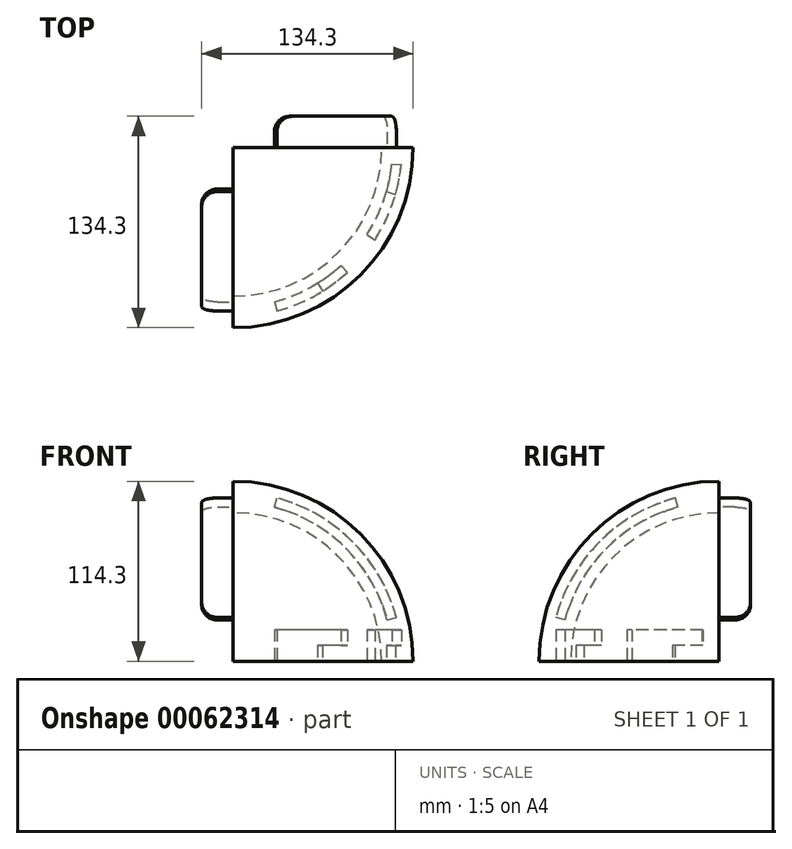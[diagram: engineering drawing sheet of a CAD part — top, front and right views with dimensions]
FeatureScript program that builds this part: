
annotation { "Feature Type Name" : "Feature", "Feature Type Description" : "" }
export const myFeature = defineFeature(function(context is Context, id is Id, definition is map)
    precondition{}
    {
        {
            var Q0;
            Q0=qCreatedBy(makeId("Right.planeOp"),FACE);
            var sketch = newSketch(context, id + "F0", { "sketchPlane" : qUnion([Q0])});
            skArc(sketch, "E0", {"start": v(0, 114.3) * mm, "mid": v(-80.82, 80.82) * mm, "end": v(-114.3, 0) * mm});
            skArc(sketch, "E1", {"start": v(0, 94.3) * mm, "mid": v(-66.68, 66.68) * mm, "end": v(-94.3, 0) * mm});
            skLineSegment(sketch, "E2", {"start": v(0, 94.3) * mm, "end": v(0, 114.3) * mm});
            skLineSegment(sketch, "E3", {"start": v(-94.3, 0) * mm, "end": v(-114.3, 0) * mm});
            skSolve(sketch);
        }
        {
            var Q0;
            Q0=makeQuery(id+"F0.imprint","IMPRINT",FACE,{"disambiguationData":[TD([[makeQuery(id+"F0.imprint","IMPRINT",EDGE,{"derivedFrom":sQuery(id+"F0.wireOp",EDGE,"E0")}),1.0]])]});
            var Q1;
            Q1=sQuery(id+"F0.wireOp",EDGE,"E2");
            revolve(context, id + "F1", {"entities" : qUnion([Q0]), "axis" : qUnion([Q1]), "revolveType" : RevolveType.ONE_DIRECTION, "angle" : 90 * degree});
        }
        {
            var Q0;
            Q0=makeQuery(id+"F1.opRevolve","CAP_FACE",FACE,{"disambiguationData":[OSD([sQuery(id+"F0.wireOp",EDGE,"E0"),sQuery(id+"F0.wireOp",EDGE,"E1"),sQuery(id+"F0.wireOp",EDGE,"E2"),sQuery(id+"F0.wireOp",EDGE,"E3")])],"isStart":false});
            var sketch = newSketch(context, id + "F2", { "sketchPlane" : qUnion([Q0])});
            skArc(sketch, "E4", {"start": v(-27.77, 103.64) * mm, "mid": v(-75.87, 75.87) * mm, "end": v(-103.64, 27.77) * mm});
            skArc(sketch, "E5", {"start": v(-26.22, 97.85) * mm, "mid": v(-71.63, 71.63) * mm, "end": v(-97.85, 26.22) * mm});
            skLineSegment(sketch, "E6", {"start": v(0, 0) * mm, "end": v(-27.77, 103.64) * mm});
            skLineSegment(sketch, "E7", {"start": v(-97.85, 26.22) * mm, "end": v(-103.64, 27.77) * mm});
            skSolve(sketch);
        }
        {
            var Q0;
            Q0=makeQuery(id+"F2.imprint","IMPRINT",FACE,{"disambiguationData":[TD([[makeQuery(id+"F2.imprint","IMPRINT",EDGE,{"derivedFrom":sQuery(id+"F2.wireOp",EDGE,"E4")}),1.0]])]});
            extrude(context, id + "F3", {"entities" : qUnion([Q0]), "operationType" : NewBodyOperationType.ADD, "depth" : 20 * mm});
        }
        {
            var Q0;
            Q0=makeQuery(id+"F0.imprint","IMPRINT",FACE,{"disambiguationData":[TD([[makeQuery(id+"F0.imprint","IMPRINT",EDGE,{"derivedFrom":sQuery(id+"F0.wireOp",EDGE,"E0")}),1.0]])]});
            var sketch = newSketch(context, id + "F4", { "sketchPlane" : qUnion([Q0])});
            skArc(sketch, "E8.0", {"start": v(-26.22, 97.85) * mm, "mid": v(-71.63, 71.63) * mm, "end": v(-97.85, 26.22) * mm});
            skArc(sketch, "E9.0", {"start": v(-27.77, 103.64) * mm, "mid": v(-75.87, 75.87) * mm, "end": v(-103.64, 27.77) * mm});
            skLineSegment(sketch, "E10", {"start": v(-26.22, 97.85) * mm, "end": v(-27.77, 103.64) * mm});
            skLineSegment(sketch, "E11", {"start": v(-97.85, 26.22) * mm, "end": v(-103.64, 27.77) * mm});
            skSolve(sketch);
        }
        {
            var Q0;
            Q0=makeQuery(id+"F4.imprint","IMPRINT",FACE,{"disambiguationData":[TD([[makeQuery(id+"F4.imprint","IMPRINT",EDGE,{"derivedFrom":sQuery(id+"F4.wireOp",EDGE,"E8.0")}),-1.0]])]});
            extrude(context, id + "F5", {"entities" : qUnion([Q0]), "operationType" : NewBodyOperationType.ADD, "oppositeDirection" : true, "depth" : 20 * mm});
        }
        {
            var Q0;
            Q0=makeQuery(id+"F5.boolean.opBoolean","MERGE",FACE,{"derivedFrom":[makeQuery(id+"F3.boolean.opBoolean","MERGE",FACE,{"derivedFrom":[makeQuery(id+"F1.opRevolve","SWEPT_FACE",FACE,{"disambiguationData":[OSD([sQuery(id+"F0.wireOp",EDGE,"E3")])]}),makeQuery(id+"F3.opExtrude","SWEPT_FACE",FACE,{"disambiguationData":[OSD([sQuery(id+"F2.wireOp",EDGE,"tj54Cu89-9J1S-AJKw-QeEM-ljXHSpR1f2pj")])]})]}),makeQuery(id+"F5.opExtrude","SWEPT_FACE",FACE,{"disambiguationData":[OSD([sQuery(id+"F4.wireOp",EDGE,"EMUQLBOC-9Rso-lLbz-JRUg-i4oPmn0DbPj1")])]})]});
            var sketch = newSketch(context, id + "F6", { "sketchPlane" : qUnion([Q0])});
            skArc(sketch, "E12", {"start": v(97.38, 27.92) * mm, "mid": v(92.18, 42) * mm, "end": v(84.96, 55.17) * mm});
            skArc(sketch, "E13", {"start": v(103.14, 29.58) * mm, "mid": v(97.64, 44.5) * mm, "end": v(89.99, 58.44) * mm});
            skLineSegment(sketch, "E14", {"start": v(26.22, 97.85) * mm, "end": v(27.77, 103.64) * mm});
            skLineSegment(sketch, "E15", {"start": v(53.68, 85.9) * mm, "end": v(56.86, 91) * mm});
            skLineSegment(sketch, "E16", {"start": v(84.96, 55.17) * mm, "end": v(89.99, 58.44) * mm});
            skLineSegment(sketch, "E17", {"start": v(97.38, 27.92) * mm, "end": v(103.14, 29.58) * mm});
            skArc(sketch, "E18.trimOffspring", {"start": v(53.68, 85.9) * mm, "mid": v(40.4, 92.9) * mm, "end": v(26.22, 97.85) * mm});
            skArc(sketch, "E19.trimOffspring", {"start": v(56.86, 91) * mm, "mid": v(42.79, 98.4) * mm, "end": v(27.77, 103.64) * mm});
            skSolve(sketch);
        }
        {
            var Q0;
            Q0=makeQuery(id+"F6.imprint","IMPRINT",FACE,{"disambiguationData":[TD([[makeQuery(id+"F6.imprint","IMPRINT",EDGE,{"derivedFrom":sQuery(id+"F6.wireOp",EDGE,"E14")}),-1.0]])]});
            var Q1;
            Q1=makeQuery(id+"F6.imprint","IMPRINT",FACE,{"disambiguationData":[TD([[makeQuery(id+"F6.imprint","IMPRINT",EDGE,{"derivedFrom":sQuery(id+"F6.wireOp",EDGE,"E12")}),-1.0]])]});
            extrude(context, id + "F7", {"entities" : qUnion([Q0, Q1]), "operationType" : NewBodyOperationType.REMOVE, "oppositeDirection" : true, "depth" : 20 * mm});
        }
        {
            var Q0;
            Q0=makeQuery(id+"F3.opExtrude","CAP_EDGE",EDGE,{"disambiguationData":[OSD([sQuery(id+"F2.wireOp",EDGE,"E7")])],"isStart":false});
            var Q1;
            Q1=makeQuery(id+"F3.opExtrude","CAP_EDGE",EDGE,{"disambiguationData":[OSD([sQuery(id+"F2.wireOp",EDGE,"E6")])],"isStart":false});
            var Q2;
            Q2=makeQuery(id+"F5.opExtrude","CAP_EDGE",EDGE,{"disambiguationData":[OSD([sQuery(id+"F4.wireOp",EDGE,"E10")])],"isStart":false});
            var Q3;
            Q3=makeQuery(id+"F5.opExtrude","CAP_EDGE",EDGE,{"disambiguationData":[OSD([sQuery(id+"F4.wireOp",EDGE,"E11")])],"isStart":false});
            fillet(context, id + "F8", {"entities" : qUnion([Q0, Q1, Q2, Q3]), "radius" : 10 * mm, "tangentPropagation" : true, "allowEdgeOverflow" : false});
        }
        {
            var Q0;
            Q0=makeQuery(id+"F6.imprint","IMPRINT",FACE,{"disambiguationData":[TD([[makeQuery(id+"F6.imprint","IMPRINT",EDGE,{"derivedFrom":sQuery(id+"F6.wireOp",EDGE,"E12")}),1.0]])]});
            cPlane(context, id + "F9", {"entities" : qUnion([Q0]), "cplaneType" : CPlaneType.OFFSET, "offset" : 10 * mm, "oppositeDirection" : true, "width" : 150 * mm, "height" : 150 * mm});
        }
        {
            var Q0;
            Q0=qCreatedBy(id+"F9.planeOp",FACE);
            var sketch = newSketch(context, id + "F10", { "sketchPlane" : qUnion([Q0])});
            skArc(sketch, "E20", {"start": v(100.79, 10.2) * mm, "mid": v(99.48, 19.14) * mm, "end": v(97.38, 27.92) * mm});
            skArc(sketch, "E21", {"start": v(106.76, 10.77) * mm, "mid": v(105.37, 20.25) * mm, "end": v(103.14, 29.58) * mm});
            skLineSegment(sketch, "E22", {"start": v(0, 0) * mm, "end": v(0.33, 0.52) * mm});
            skLineSegment(sketch, "E23", {"start": v(0, 0) * mm, "end": v(0.5, 0.54) * mm});
            skLineSegment(sketch, "E24", {"start": v(0, 0) * mm, "end": v(2.58, 0.74) * mm});
            skLineSegment(sketch, "E25", {"start": v(-5.11, 0) * mm, "end": v(2.58, 0.74) * mm});
            skLineSegment(sketch, "E26.trimOffspring", {"start": v(53.68, 85.9) * mm, "end": v(56.86, 91) * mm});
            skLineSegment(sketch, "E27.trimOffspring", {"start": v(68.44, 74.69) * mm, "end": v(72.5, 79.1) * mm});
            skLineSegment(sketch, "E28.trimOffspring", {"start": v(97.38, 27.92) * mm, "end": v(103.14, 29.58) * mm});
            skLineSegment(sketch, "E29.trimOffspring", {"start": v(100.79, 10.2) * mm, "end": v(106.76, 10.77) * mm});
            skArc(sketch, "E30.trimOffspring", {"start": v(68.44, 74.69) * mm, "mid": v(61.32, 80.64) * mm, "end": v(53.68, 85.9) * mm});
            skArc(sketch, "E31.trimOffspring", {"start": v(72.5, 79.1) * mm, "mid": v(64.95, 85.41) * mm, "end": v(56.86, 91) * mm});
            skSolve(sketch);
        }
        {
            var Q0;
            Q0=qSketchRegion(id+"F10",true);
            extrude(context, id + "F11", {"entities" : qUnion([Q0]), "operationType" : NewBodyOperationType.REMOVE, "oppositeDirection" : true, "depth" : 10 * mm});
        }
    });
